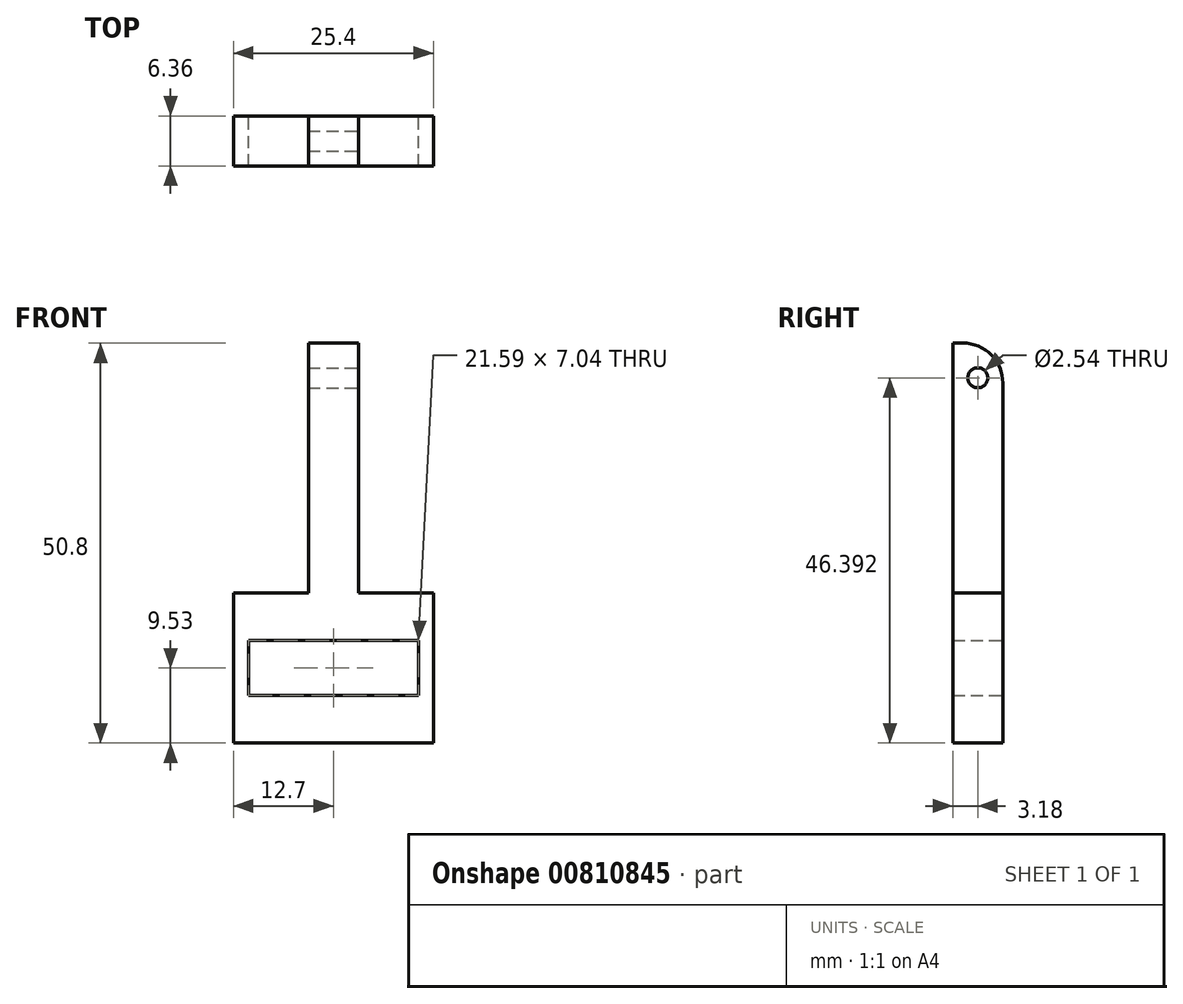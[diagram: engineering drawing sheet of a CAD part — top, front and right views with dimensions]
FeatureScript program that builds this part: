
annotation { "Feature Type Name" : "Feature", "Feature Type Description" : "" }
export const myFeature = defineFeature(function(context is Context, id is Id, definition is map)
    precondition{}
    {
        {
            var Q0;
            Q0=qCreatedBy(makeId("Front.planeOp"),FACE);
            var sketch = newSketch(context, id + "F0", { "sketchPlane" : qUnion([Q0])});
            skLineSegment(sketch, "E0.bottom", {"start": v(-3.18, 41.28) * mm, "end": v(3.18, 41.28) * mm});
            skLineSegment(sketch, "E0.top", {"start": v(-3.18, 9.53) * mm, "end": v(3.18, 9.53) * mm});
            skLineSegment(sketch, "E0.left", {"start": v(-3.18, 41.28) * mm, "end": v(-3.17, 9.53) * mm});
            skLineSegment(sketch, "E0.right", {"start": v(3.18, 41.28) * mm, "end": v(3.17, 9.53) * mm});
            skLineSegment(sketch, "E1.bottom", {"start": v(-12.7, 9.53) * mm, "end": v(12.7, 9.53) * mm});
            skLineSegment(sketch, "E1.top", {"start": v(-12.7, -9.53) * mm, "end": v(12.7, -9.53) * mm});
            skLineSegment(sketch, "E1.left", {"start": v(-12.7, 9.53) * mm, "end": v(-12.7, -9.53) * mm});
            skLineSegment(sketch, "E1.right", {"start": v(12.7, 9.53) * mm, "end": v(12.7, -9.53) * mm});
            skPoint(sketch, "E1.middle", {"position": v(0, 0) * mm});
            skPoint(sketch, "E1.middle.positionSnap0", {"position": v(0, 9.53) * mm});
            skPoint(sketch, "E1.centerSnap0", {"position": v(0, 9.53) * mm});
            skSolve(sketch);
        }
        {
            var Q0;
            Q0 = qSketchRegion(id + "F0", true);
            extrude(context, id + "F1", {"entities" : qUnion([Q0]), "endBound" : BoundingType.SYMMETRIC, "depth" : 6.35 * mm, "offsetDistance" : 25.4 * mm});
        }
        {
            var Q0;
            Q0=makeQuery(id+"F1.opExtrude","CAP_EDGE",EDGE,{"disambiguationData":[OSD([sQuery(id+"F0.wireOp",EDGE,"E0.bottom")])],"isStart":true});
            fillet(context, id + "F2", {"entities" : qUnion([Q0]), "radius" : 5.08 * mm, "tangentPropagation" : true, "allowEdgeOverflow" : false});
        }
        {
            var Q0;
            Q0=makeQuery(id+"F1.opExtrude","SWEPT_FACE",FACE,{"disambiguationData":[OSD([sQuery(id+"F0.wireOp",EDGE,"E0.right")])]});
            var sketch = newSketch(context, id + "F3", { "sketchPlane" : qUnion([Q0])});
            skCircle(sketch, "E2", {"center": v(0, 36.86) * mm, "radius": 1.27 * mm});
            skSolve(sketch);
        }
        {
            var Q0;
            Q0=makeQuery(id+"F3.imprint","IMPRINT",FACE,{"disambiguationData":[TD([[makeQuery(id+"F3.imprint","IMPRINT",EDGE,{"derivedFrom":sQuery(id+"F3.wireOp",EDGE,"E2")}),1.0]])]});
            extrude(context, id + "F4", {"entities" : qUnion([Q0]), "operationType" : NewBodyOperationType.REMOVE, "oppositeDirection" : true, "depth" : 53.34 * mm, "offsetDistance" : 25.4 * mm});
        }
        {
            var Q0;
            Q0=makeQuery(id+"F1.opExtrude","CAP_FACE",FACE,{"disambiguationData":[OSD([sQuery(id+"F0.wireOp",EDGE,"E0.bottom"),sQuery(id+"F0.wireOp",EDGE,"E0.left"),sQuery(id+"F0.wireOp",EDGE,"E0.right"),sQuery(id+"F0.wireOp",EDGE,"E1.bottom"),sQuery(id+"F0.wireOp",EDGE,"E1.top"),sQuery(id+"F0.wireOp",EDGE,"E1.left"),sQuery(id+"F0.wireOp",EDGE,"E1.right")])],"isStart":false});
            var sketch = newSketch(context, id + "F5", { "sketchPlane" : qUnion([Q0])});
            skLineSegment(sketch, "E3.bottom", {"start": v(10.8, 3.52) * mm, "end": v(-10.8, 3.52) * mm});
            skLineSegment(sketch, "E3.top", {"start": v(10.8, -3.52) * mm, "end": v(-10.8, -3.52) * mm});
            skLineSegment(sketch, "E3.left", {"start": v(10.8, 3.52) * mm, "end": v(10.8, -3.52) * mm});
            skLineSegment(sketch, "E3.right", {"start": v(-10.8, 3.52) * mm, "end": v(-10.8, -3.52) * mm});
            skPoint(sketch, "E3.middle", {"position": v(0, 0) * mm});
            skSolve(sketch);
        }
        {
            var Q0;
            Q0=makeQuery(id+"F5.imprint","IMPRINT",FACE,{"disambiguationData":[TD([[makeQuery(id+"F5.imprint","IMPRINT",EDGE,{"derivedFrom":sQuery(id+"F5.wireOp",EDGE,"E3.bottom")}),1.0]])]});
            extrude(context, id + "F6", {"entities" : qUnion([Q0]), "operationType" : NewBodyOperationType.REMOVE, "endBound" : BoundingType.SYMMETRIC, "depth" : 50.8 * mm, "offsetDistance" : 25.4 * mm});
        }
    });
